# Revit family: Vitra_İntegra_Semi-recessedWashBasin_ 7069B003-0001
name_source: partatom
category: Plumbing Fixtures
revit_build: Autodesk Revit 2017 (Build: 20160225_1515(x64)
units: mm (PartAtom-declared; Revit-internal decimal feet)

## family parameters
Cut with Voids When Loaded = No
Host = Face
OmniClass Number = 23.45.05.14.14
OmniClass Title = Sinks/Lavatories
Part Type = Normal
Room Calculation Point = No
Round Connector Dimension = Use Diameter
Shared = Yes

## types (2) — shared parameters
BIMobject category = Sanitary - Basins
CW Connection = No
Color = White
Default Elevation = 850 mm  [stored 2.78871 ft]
Design country = Turkey
HW Connection = No
IFC Classification = Sanitary Terminal
Main Material = Ceramic
Manufacturer = Vitra
Manufacturer name = Vitra
Masterformat 2014 Code = 22 41 16
Masterformat 2014 Description = Residential Lavatories and Sinks
MountingType = Wall Mounted
NBS Referans Code = 35-65-70-94
NBS Referans Description = Wash Basin Systems
Nominal Depth = 450 mm  [stored 1.47638 ft]
NominalHeight = 165 mm
NominalWidth = 550 mm
OmniClass Code = 23.45.05.14.14
OmniClass Description = Sinks/Lavatories
Product certification = https://vitraglobal.com
Product family = Wall Mounted WashBasin
Product group = İntegra
Secondary Material = Vitra-Ceramic-White
UNSPSC Code = 301815
URL = https://vitraglobal.com
Uniclass 1.4 Code = L7212
Uniclass 1.4 Description = Washbasins
Uniclass 2.0 Code = SS-35-65-70-94
Uniclass 2.0 Description = Sanitary Dispensing And Disposal Units
Uniclass 2015 Code = Pr_40_20_96_81
Uniclass 2015 Name = Wash basins, Sinks and troughs
Uniformat II Code = D2010
Uniformat II Description = Plumbing Fixtures
Vent Connection = No
Warranty Period (Year) = 10 Years
Waste Connection = Yes
Weight Net (kg) = 17,084
Youtube = https://www.youtube.com
zero-valued in all types: Cost

## per-type parameters (varying)
| type | Article No. (default) | Description | Model | Product SKU | Product data url |
| WashBasin-Vitra_İntegra_7069B003-0001 | 7069B003-0001 | VitrA İntegra Semi-recessed basin 55 cm, Semi-recessed basin, With tap hole, with overflow hole | 7069B003-0001 | 7069B003-0001 | https://www.vitra.com.tr |
| WashBasin-Vitra_İntegra_7069B403-0001 | 7069B403-0001 | VitrA İntegra Semi-recessed basin 55 cm, Semi-recessed basin, With tap hole, with overflow hole, with VitrA Clean | 7069B403-0001 | 7069B403-0001 | https://www.vitraglobal.com |

note: [stored X ft] marks values corroborated as IEEE doubles in the binary element streams (Revit-internal decimal feet)

## geometry (parser evidence)
native form markers: Sweep x3
no freeform markers — native parametric forms only
